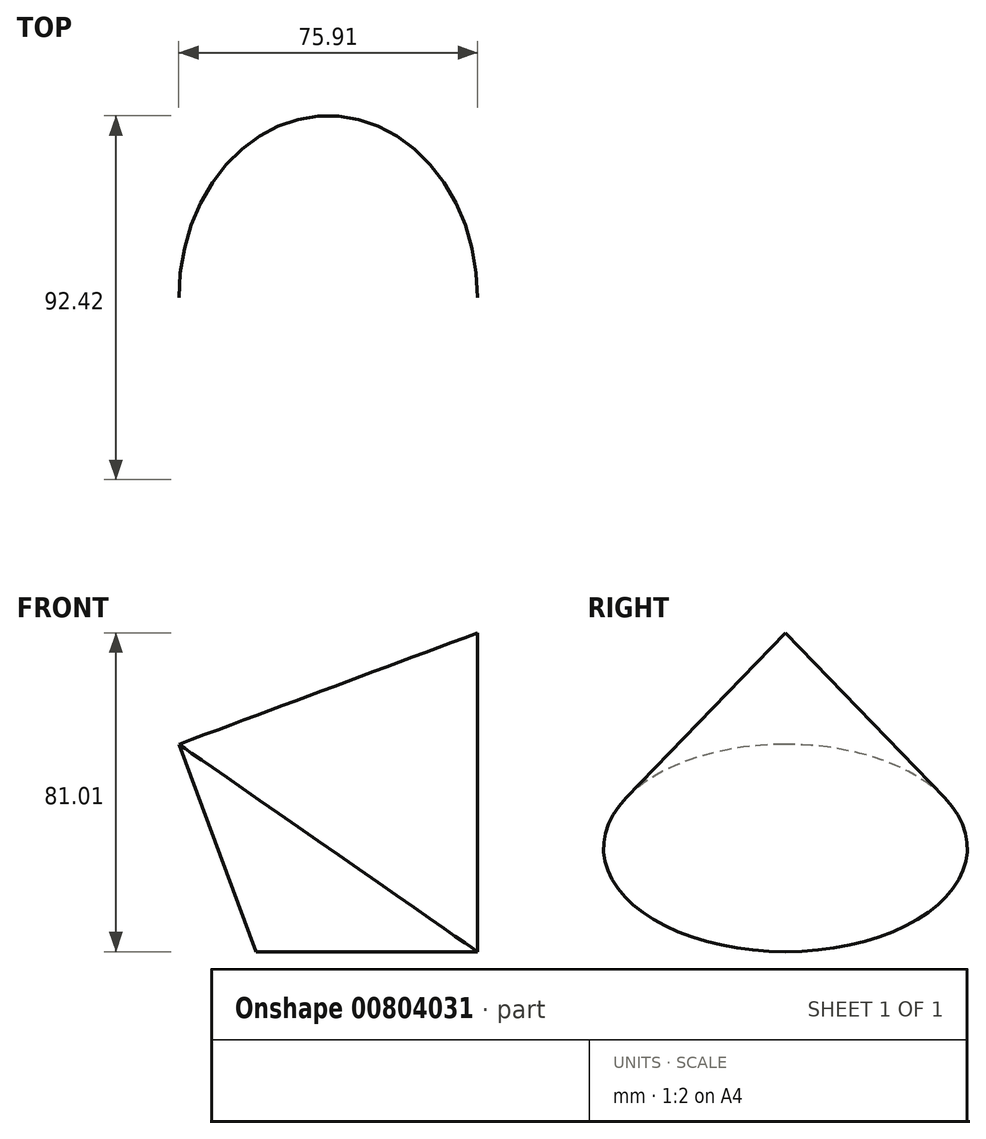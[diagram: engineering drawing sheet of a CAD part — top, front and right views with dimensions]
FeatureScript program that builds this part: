
annotation { "Feature Type Name" : "Feature", "Feature Type Description" : "" }
export const myFeature = defineFeature(function(context is Context, id is Id, definition is map)
    precondition{}
    {
        {
            var Q0;
            Q0=qCreatedBy(makeId("Front.planeOp"),FACE);
            var sketch = newSketch(context, id + "F0", { "sketchPlane" : qUnion([Q0])});
            skLineSegment(sketch, "E0.bottom", {"start": v(-34.34, 46.95) * mm, "end": v(21.92, 46.95) * mm});
            skLineSegment(sketch, "E0.top", {"start": v(-34.34, -49.14) * mm, "end": v(21.92, -49.14) * mm});
            skLineSegment(sketch, "E0.left", {"start": v(-34.34, 46.95) * mm, "end": v(-34.34, -49.14) * mm});
            skLineSegment(sketch, "E0.right", {"start": v(21.92, 46.95) * mm, "end": v(21.92, -49.14) * mm});
            skLineSegment(sketch, "E1", {"start": v(44.57, 64.48) * mm, "end": v(-34.34, -49.14) * mm});
            skSolve(sketch);
        }
        {
            var Q0;
            {var subQ0=sQuery(id+"F0.wireOp",EDGE,"E0.top");Q0=makeQuery(id+"F0.imprint","IMPRINT",FACE,{"disambiguationData":[TD([[makeQuery(id+"F0.imprint","IMPRINT",EDGE,{"derivedFrom":subQ0}),1.0]])]});}
            var Q1;
            Q1=sQuery(id+"F0.wireOp",EDGE,"E1");
            revolve(context, id + "F1", {"surfaceOperationType" : NewSurfaceOperationType.NEW, "entities" : qUnion([Q0]), "axis" : qUnion([Q1]), "revolveType" : RevolveType.FULL});
        }
    });
